# Revit family: 1 SOUND_Cannon_C8
name_source: partatom
category: Communication Devices
units: mm (PartAtom-declared; Revit-internal decimal feet)

## family parameters
Always vertical = No
Cut with Voids When Loaded = No
Maintain Annotation Orientation = No
Part Type = Normal
Room Calculation Point = No
Round Connector Dimension = Use Diameter
Shared = No
Work Plane-Based = Yes

## types (2) — shared parameters
Bandwidth = 55 Hz - 18 kHz (-6 dB)
Construction = Finland birch plywood (urea glue), polyurea, matte salt and UV resistant coating, 316 stainless steel hardware, 3D spacer mesh fabric
Default Elevation = 1219 mm
Depth - Overall = 260 mm
Dimensions (HxWxD) = 10.2” (260 mm) x 10.2” (260 mm) x 10.2” (260 mm)
Height Overall = 260 mm
Impedance = 8Ω
Manufacturer = 1 Sound
Power = 400 watts (program), 200 watts (AES)
Rigging = (4) M6 points
URL = https://www.1-sound.com
Weight = 18.4 lb / 8.3 kg
Width - Overall = 260 mm

## per-type parameters (varying)
| type | Connector - NL4 | Connector - Screw Terminal Block | Connectors |
| C8i | No | Yes | (1) screw terminal block with input +/- and loop +/- |
| C8 | Yes | No | (2) NL4, 2-circuit switch, (1) Neutric NDL dummyPlug |

note: column(s) folded — value = type name in every type: Model

## geometry (parser evidence)
native form markers: Sweep x12
no freeform markers — native parametric forms only
